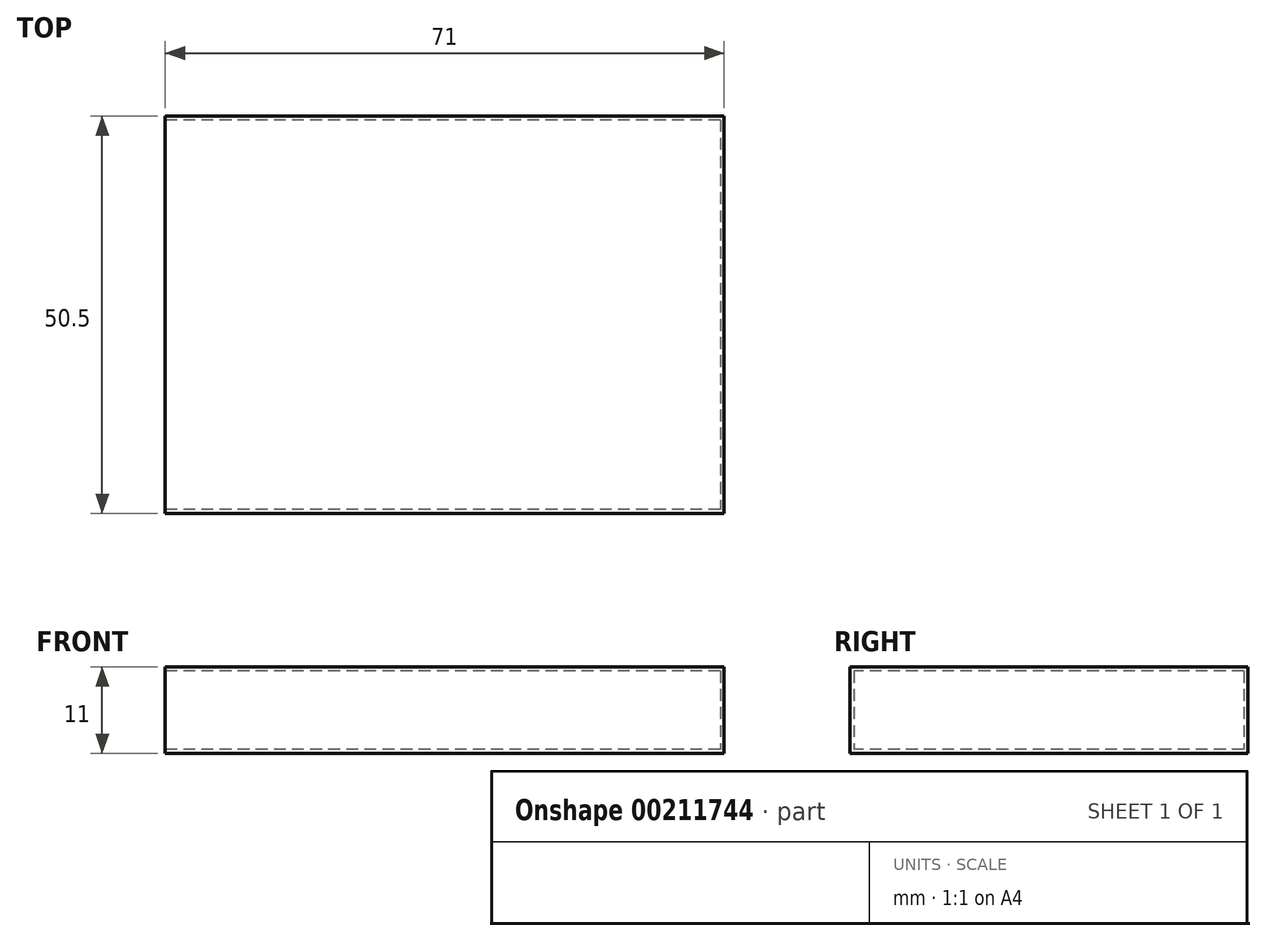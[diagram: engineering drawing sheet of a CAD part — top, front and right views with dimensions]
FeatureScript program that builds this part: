
annotation { "Feature Type Name" : "Feature", "Feature Type Description" : "" }
export const myFeature = defineFeature(function(context is Context, id is Id, definition is map)
    precondition{}
    {
        {
            var Q0;
            Q0=qCreatedBy(makeId("Front.planeOp"),FACE);
            var sketch = newSketch(context, id + "F0", { "sketchPlane" : qUnion([Q0])});
            skLineSegment(sketch, "E0.bottom", {"start": v(35.5, 5.5) * mm, "end": v(-35.5, 5.5) * mm});
            skLineSegment(sketch, "E0.top", {"start": v(35.5, -5.5) * mm, "end": v(-35.5, -5.5) * mm});
            skLineSegment(sketch, "E0.left", {"start": v(35.5, 5.5) * mm, "end": v(35.5, -5.5) * mm});
            skLineSegment(sketch, "E0.right", {"start": v(-35.5, 5.5) * mm, "end": v(-35.5, -5.5) * mm});
            skSolve(sketch);
        }
        {
            var Q0;
            Q0=makeQuery(id+"F0.imprint","IMPRINT",FACE,{"disambiguationData":[TD([[makeQuery(id+"F0.imprint","IMPRINT",EDGE,{"derivedFrom":sQuery(id+"F0.wireOp",EDGE,"E0.bottom")}),1.0]])]});
            extrude(context, id + "F1", {"entities" : qUnion([Q0]), "endBound" : BoundingType.SYMMETRIC, "oppositeDirection" : true, "depth" : 50.5 * mm});
        }
        {
            var Q0;
            Q0=makeQuery(id+"F1.opExtrude","SWEPT_FACE",FACE,{"disambiguationData":[OSD([sQuery(id+"F0.wireOp",EDGE,"E0.right")])]});
            shell(context, id + "F2", {"entities" : qUnion([Q0]), "thickness" : 0.5 * mm});
        }
    });
